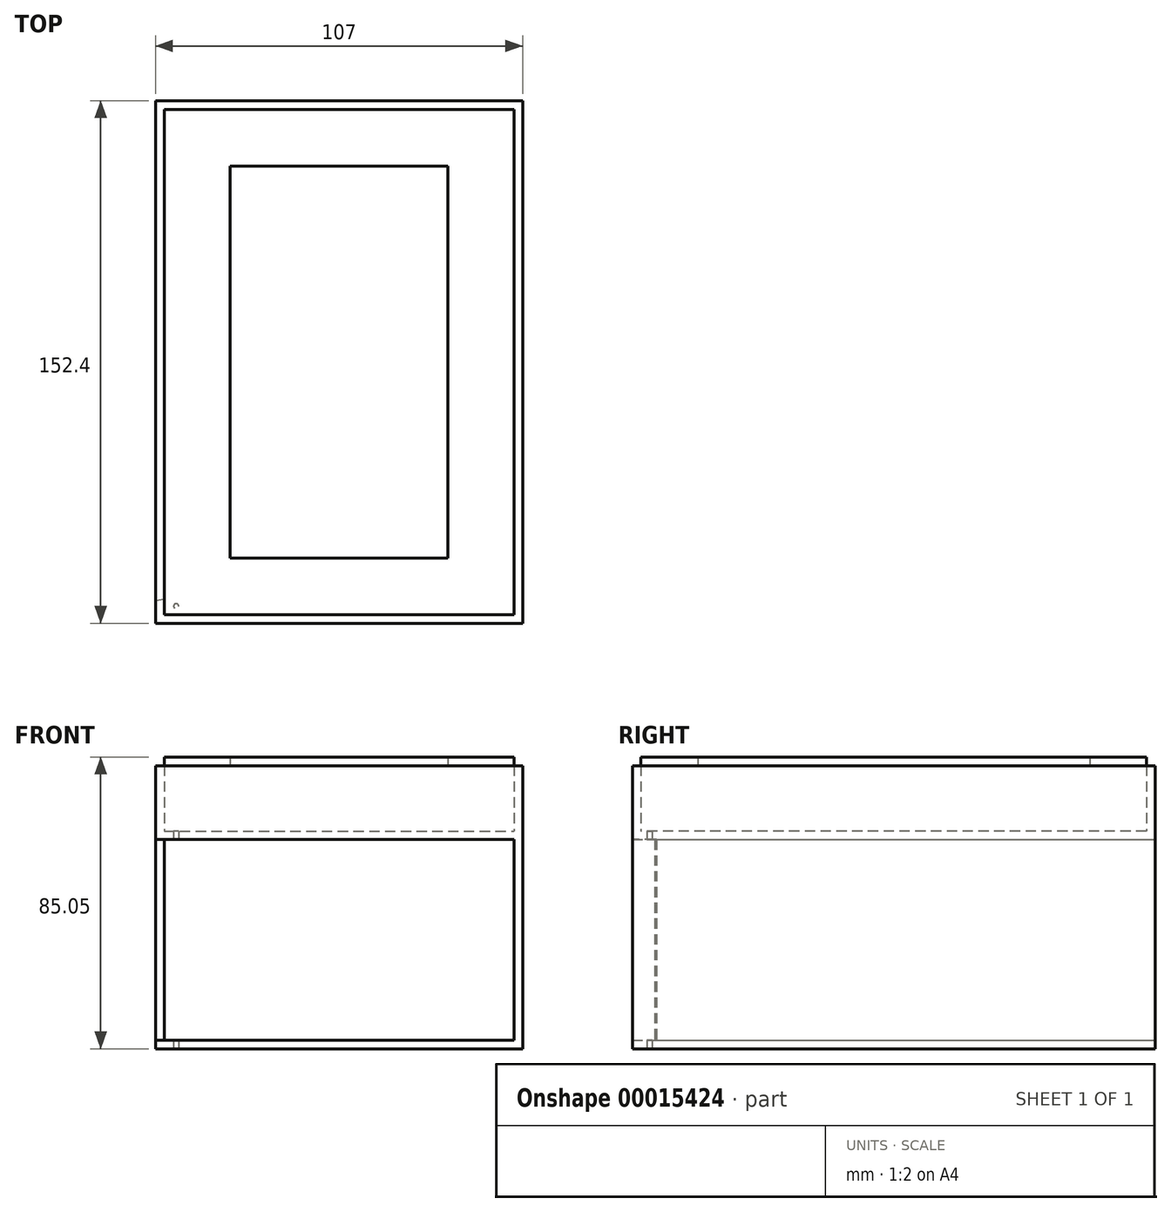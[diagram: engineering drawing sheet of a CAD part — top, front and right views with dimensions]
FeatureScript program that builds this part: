
annotation { "Feature Type Name" : "Feature", "Feature Type Description" : "" }
export const myFeature = defineFeature(function(context is Context, id is Id, definition is map)
    precondition{}
    {
        {
            var Q0;
            Q0=qCreatedBy(makeId("Top.planeOp"),FACE);
            var sketch = newSketch(context, id + "F0", { "sketchPlane" : qUnion([Q0])});
            skLineSegment(sketch, "E0.bottom", {"start": v(-35.06, -76.54) * mm, "end": v(71.94, -76.54) * mm});
            skLineSegment(sketch, "E0.top", {"start": v(-35.06, 75.86) * mm, "end": v(71.94, 75.86) * mm});
            skLineSegment(sketch, "E0.left", {"start": v(-35.06, -76.54) * mm, "end": v(-35.06, 75.86) * mm});
            skLineSegment(sketch, "E0.right", {"start": v(71.94, -76.54) * mm, "end": v(71.94, 75.86) * mm});
            skCircle(sketch, "E1", {"center": v(-29.06, -71.54) * mm, "radius": 0.75 * mm});
            skSolve(sketch);
        }
        {
            var Q0;
            Q0=makeQuery(id+"F0.imprint","IMPRINT",FACE,{"disambiguationData":[TD([[makeQuery(id+"F0.imprint","IMPRINT",EDGE,{"derivedFrom":sQuery(id+"F0.wireOp",EDGE,"E0.bottom")}),1.0]])]});
            extrude(context, id + "F1", {"entities" : qUnion([Q0]), "depth" : 63.5 * mm});
        }
        {
            var Q0;
            Q0=makeQuery(id+"F1.opExtrude","CAP_FACE",FACE,{"disambiguationData":[OSD([sQuery(id+"F0.wireOp",EDGE,"E0.bottom"),sQuery(id+"F0.wireOp",EDGE,"E0.top"),sQuery(id+"F0.wireOp",EDGE,"E0.left"),sQuery(id+"F0.wireOp",EDGE,"E0.right")])],"isStart":false});
            var sketch = newSketch(context, id + "F2", { "sketchPlane" : qUnion([Q0])});
            skLineSegment(sketch, "E2.bottom", {"start": v(-35.06, -76.54) * mm, "end": v(71.94, -76.54) * mm});
            skLineSegment(sketch, "E2.top", {"start": v(-35.06, 75.86) * mm, "end": v(71.94, 75.86) * mm});
            skLineSegment(sketch, "E2.left", {"start": v(-35.06, -76.54) * mm, "end": v(-35.06, 75.86) * mm});
            skLineSegment(sketch, "E2.right", {"start": v(71.94, -76.54) * mm, "end": v(71.94, 75.86) * mm});
            skSolve(sketch);
        }
        {
            var Q0;
            Q0=makeQuery(id+"F1.opExtrude","SWEPT_FACE",FACE,{"disambiguationData":[OSD([sQuery(id+"F0.wireOp",EDGE,"E0.bottom")])]});
            var Q1;
            Q1=makeQuery(id+"F1.opExtrude","SWEPT_FACE",FACE,{"disambiguationData":[OSD([sQuery(id+"F0.wireOp",EDGE,"E0.top")])]});
            var Q2;
            Q2=makeQuery(id+"F1.opExtrude","SWEPT_FACE",FACE,{"disambiguationData":[OSD([sQuery(id+"F0.wireOp",EDGE,"E1")])]});
            shell(context, id + "F3", {"entities" : qUnion([Q0, Q1, Q2]), "thickness" : 2.5 * mm});
        }
        {
            var Q0;
            Q0=makeQuery(id+"F2.imprint","IMPRINT",FACE,{"disambiguationData":[TD([[makeQuery(id+"F2.imprint","IMPRINT",EDGE,{"derivedFrom":sQuery(id+"F2.wireOp",EDGE,"E2.bottom")}),1.0]])]});
            extrude(context, id + "F4", {"entities" : qUnion([Q0]), "operationType" : NewBodyOperationType.ADD, "depth" : 19.05 * mm});
        }
        {
            var Q0;
            Q0=makeQuery(id+"F4.opExtrude","CAP_FACE",FACE,{"disambiguationData":[OSD([sQuery(id+"F2.wireOp",EDGE,"E2.bottom"),sQuery(id+"F2.wireOp",EDGE,"E2.top"),sQuery(id+"F2.wireOp",EDGE,"E2.left"),sQuery(id+"F2.wireOp",EDGE,"E2.right")])],"isStart":false});
            var Q1;
            {var subQ0=sQuery(id+"F0.wireOp",EDGE,"E1");Q1=makeQuery(id+"F4.boolean.opBoolean","MERGE",FACE,{"derivedFrom":[makeQuery(id+"F1.opExtrude","SWEPT_FACE",FACE,{"disambiguationData":[OSD([subQ0])]}),makeQuery(id+"F4.opExtrude","SWEPT_FACE",FACE,{"disambiguationData":[OSD([subQ0])]})]});}
            shell(context, id + "F5", {"entities" : qUnion([Q0, Q1]), "thickness" : 2.5 * mm});
        }
        {
            var Q0;
            Q0=makeQuery(id+"F4.opExtrude","CAP_FACE",FACE,{"disambiguationData":[OSD([sQuery(id+"F2.wireOp",EDGE,"E2.bottom"),sQuery(id+"F2.wireOp",EDGE,"E2.top"),sQuery(id+"F2.wireOp",EDGE,"E2.left"),sQuery(id+"F2.wireOp",EDGE,"E2.right")])],"isStart":false});
            var sketch = newSketch(context, id + "F6", { "sketchPlane" : qUnion([Q0])});
            skLineSegment(sketch, "E3.bottom", {"start": v(-35.06, -76.54) * mm, "end": v(71.94, -76.54) * mm});
            skLineSegment(sketch, "E3.top", {"start": v(-35.06, 75.86) * mm, "end": v(71.94, 75.86) * mm});
            skLineSegment(sketch, "E3.left", {"start": v(-35.06, -76.54) * mm, "end": v(-35.06, 75.86) * mm});
            skLineSegment(sketch, "E3.right", {"start": v(71.94, -76.54) * mm, "end": v(71.94, 75.86) * mm});
            skLineSegment(sketch, "E4.bottom", {"start": v(-13.3, -57.49) * mm, "end": v(50.2, -57.49) * mm});
            skLineSegment(sketch, "E4.top", {"start": v(-13.3, 56.81) * mm, "end": v(50.2, 56.81) * mm});
            skLineSegment(sketch, "E4.left", {"start": v(-13.3, -57.49) * mm, "end": v(-13.3, 56.81) * mm});
            skLineSegment(sketch, "E4.right", {"start": v(50.2, -57.49) * mm, "end": v(50.2, 56.81) * mm});
            skLineSegment(sketch, "E5", {"start": v(18.44, -76.54) * mm, "end": v(18.44, -57.49) * mm});
            skLineSegment(sketch, "E6", {"start": v(-13.3, -13.94) * mm, "end": v(-35.06, -13.94) * mm});
            skLineSegment(sketch, "E7", {"start": v(71.94, -12.25) * mm, "end": v(50.2, -12.25) * mm});
            skLineSegment(sketch, "E8", {"start": v(11.45, 56.81) * mm, "end": v(11.45, 75.86) * mm});
            skSolve(sketch);
        }
        {
            var Q0;
            {var subQ7=sQuery(id+"F6.wireOp",EDGE,"E4.top");var subQ9=sQuery(id+"F6.wireOp",EDGE,"E4.left");var subQ11=makeQuery(id+"F6.imprint","INTERSECT",VERTEX,{"derivedFrom":[subQ7,subQ9]});Q0=makeQuery(id+"F6.imprint","IMPRINT",FACE,{"disambiguationData":[TD([[makeQuery(id+"F6.imprint","IMPRINT",EDGE,{"disambiguationData":[TD([[subQ11,-1.0]])],"derivedFrom":subQ7}),1.0]])]});}
            var Q1;
            {var subQ7=sQuery(id+"F6.wireOp",EDGE,"E4.top");var subQ9=sQuery(id+"F6.wireOp",EDGE,"E4.right");var subQ11=makeQuery(id+"F6.imprint","INTERSECT",VERTEX,{"derivedFrom":[subQ7,subQ9]});Q1=makeQuery(id+"F6.imprint","IMPRINT",FACE,{"disambiguationData":[TD([[makeQuery(id+"F6.imprint","IMPRINT",EDGE,{"disambiguationData":[TD([[subQ11,1.0]])],"derivedFrom":subQ7}),1.0]])]});}
            var Q2;
            {var subQ7=sQuery(id+"F6.wireOp",EDGE,"E4.right");var subQ9=sQuery(id+"F6.wireOp",EDGE,"E4.bottom");var subQ11=makeQuery(id+"F6.imprint","INTERSECT",VERTEX,{"derivedFrom":[subQ9,subQ7]});Q2=makeQuery(id+"F6.imprint","IMPRINT",FACE,{"disambiguationData":[TD([[makeQuery(id+"F6.imprint","IMPRINT",EDGE,{"disambiguationData":[TD([[subQ11,1.0]])],"derivedFrom":subQ9}),-1.0]])]});}
            var Q3;
            {var subQ7=sQuery(id+"F6.wireOp",EDGE,"E4.left");var subQ9=sQuery(id+"F6.wireOp",EDGE,"E4.bottom");var subQ11=makeQuery(id+"F6.imprint","INTERSECT",VERTEX,{"derivedFrom":[subQ9,subQ7]});Q3=makeQuery(id+"F6.imprint","IMPRINT",FACE,{"disambiguationData":[TD([[makeQuery(id+"F6.imprint","IMPRINT",EDGE,{"disambiguationData":[TD([[subQ11,-1.0]])],"derivedFrom":subQ9}),-1.0]])]});}
            extrude(context, id + "F7", {"entities" : qUnion([Q0, Q1, Q2, Q3]), "depth" : 2.5 * mm});
        }
        {
            var Q0;
            Q0=makeQuery(id+"F3.opShell","OFFSET_EDGE",EDGE,{"disambiguationData":[OSD([sQuery(id+"F0.wireOp",EDGE,"E0.bottom"),sQuery(id+"F0.wireOp",EDGE,"E0.left")])]});
            chamfer(context, id + "F8", {"entities" : qUnion([Q0]), "chamferType" : ChamferType.OFFSET_ANGLE, "width" : 7 * mm, "oppositeDirection" : false, "angle" : 80 * degree, "tangentPropagation" : true});
        }
    });
